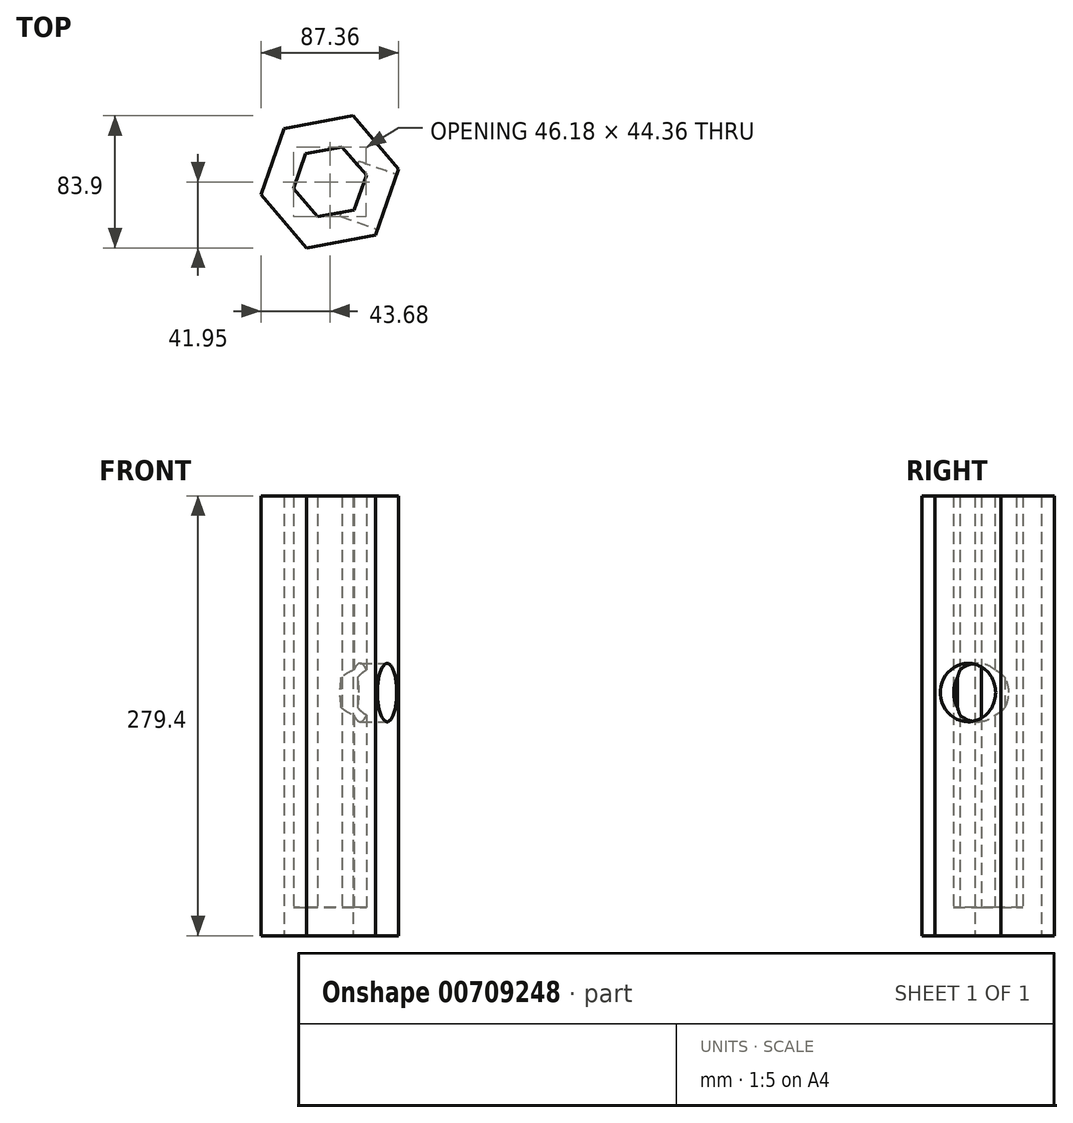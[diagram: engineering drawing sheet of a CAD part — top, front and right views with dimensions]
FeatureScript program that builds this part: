
annotation { "Feature Type Name" : "Feature", "Feature Type Description" : "" }
export const myFeature = defineFeature(function(context is Context, id is Id, definition is map)
    precondition{}
    {
        {
            var Q0;
            Q0=qCreatedBy(makeId("Top.planeOp"),FACE);
            var sketch = newSketch(context, id + "F0", { "sketchPlane" : qUnion([Q0])});
            skCircle(sketch, "E0.cCircle", {"center": v(0, 0) * mm, "radius": 38.5 * mm, "construction": true});
            skLineSegment(sketch, "E0.0", {"start": v(14.7, 41.95) * mm, "end": v(43.68, 8.25) * mm});
            skLineSegment(sketch, "E0.1", {"start": v(43.68, 8.25) * mm, "end": v(28.98, -33.7) * mm});
            skLineSegment(sketch, "E0.2", {"start": v(28.98, -33.7) * mm, "end": v(-14.7, -41.95) * mm});
            skLineSegment(sketch, "E0.3", {"start": v(-14.7, -41.95) * mm, "end": v(-43.68, -8.25) * mm});
            skLineSegment(sketch, "E0.4", {"start": v(-43.68, -8.25) * mm, "end": v(-28.98, 33.7) * mm});
            skLineSegment(sketch, "E0.5", {"start": v(-28.98, 33.7) * mm, "end": v(14.7, 41.95) * mm});
            skPoint(sketch, "E0.0.midPoint", {"position": v(29.19, 25.1) * mm});
            skSolve(sketch);
        }
        {
            var Q0;
            Q0 = qSketchRegion(id + "F0", true);
            extrude(context, id + "F1", {"entities" : qUnion([Q0]), "depth" : 279.4 * mm, "offsetDistance" : 25.4 * mm});
        }
        {
            var Q0;
            Q0=makeQuery(id+"F1.opExtrude","CAP_FACE",FACE,{"disambiguationData":[OSD([sQuery(id+"F0.wireOp",EDGE,"E0.0"),sQuery(id+"F0.wireOp",EDGE,"E0.1"),sQuery(id+"F0.wireOp",EDGE,"E0.2"),sQuery(id+"F0.wireOp",EDGE,"E0.3"),sQuery(id+"F0.wireOp",EDGE,"E0.4"),sQuery(id+"F0.wireOp",EDGE,"E0.5")])],"isStart":false});
            shell(context, id + "F2", {"entities" : qUnion([Q0]), "thickness" : 18.14 * mm});
        }
        {
            var Q0;
            Q0=makeQuery(id+"F1.opExtrude","SWEPT_FACE",FACE,{"disambiguationData":[OSD([sQuery(id+"F0.wireOp",EDGE,"E0.1")])]});
            var sketch = newSketch(context, id + "F3", { "sketchPlane" : qUnion([Q0])});
            skCircle(sketch, "E1", {"center": v(0, 154.47) * mm, "radius": 18.56 * mm});
            skSolve(sketch);
        }
        {
            var Q0;
            Q0 = qSketchRegion(id + "F3", true);
            extrude(context, id + "F4", {"entities" : qUnion([Q0]), "operationType" : NewBodyOperationType.REMOVE, "oppositeDirection" : true, "depth" : 25.4 * mm, "offsetDistance" : 25.4 * mm});
        }
    });
